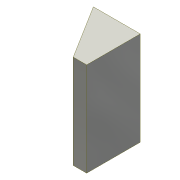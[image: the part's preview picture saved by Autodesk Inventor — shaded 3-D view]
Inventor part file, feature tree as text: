
AUTODESK INVENTOR PART (.ipt)
format: ipt  version: 2021 (Build 250183000, 183)  size: 239,616 bytes
history: native  units: mm
features: sketch x7, extrude x4, projected_geometry x4, other x3, hole x3, fillet x1, mirror x1
ambient origin geometry x8: Origin, YZ Plane, XZ Plane, XY Plane, X Axis, Y Axis, Z Axis, Center Point
bodies: Body1 (feature_tree)
feature tree (23):
  other  "Твердое тело1"
  extrude  "Выдавливание1"  Depth=140.0mm TaperAngle=0.0deg
  extrude  "Выдавливание2"  Depth=80.0mm
  hole  "Отверстие1"  [1 undecoded]
  other  "РабПлоскость1"
  extrude  "Выдавливание3"  Depth=20.0mm
  hole  "Отверстие2"  [1 undecoded]
  extrude  "Выдавливание4"  Depth=120.7mm
  fillet  "Сопряжение1"  Radius=6.5mm
  hole  "Отверстие3"  [1 undecoded]
  other  "РабПлоскость2"
  mirror  "Зеркальное отражение1"
  sketch  "Эскиз1"
  sketch  "Эскиз2"
  projected_geometry  "Спроецированная петля1"
  sketch  "Эскиз3"
  projected_geometry  "Спроецированная петля2"
  sketch  "Эскиз4"
  projected_geometry  "Спроецированная петля3"
  sketch  "Эскиз5"
  projected_geometry  "Спроецированная петля4"
  sketch  "Эскиз7"
  sketch  "Эскиз8"
note: 3 required parameter values undecoded (feature->parameter linkage not recoverable at this tier; creation-order binding heuristic only, values carry confidence <= 0.55)
